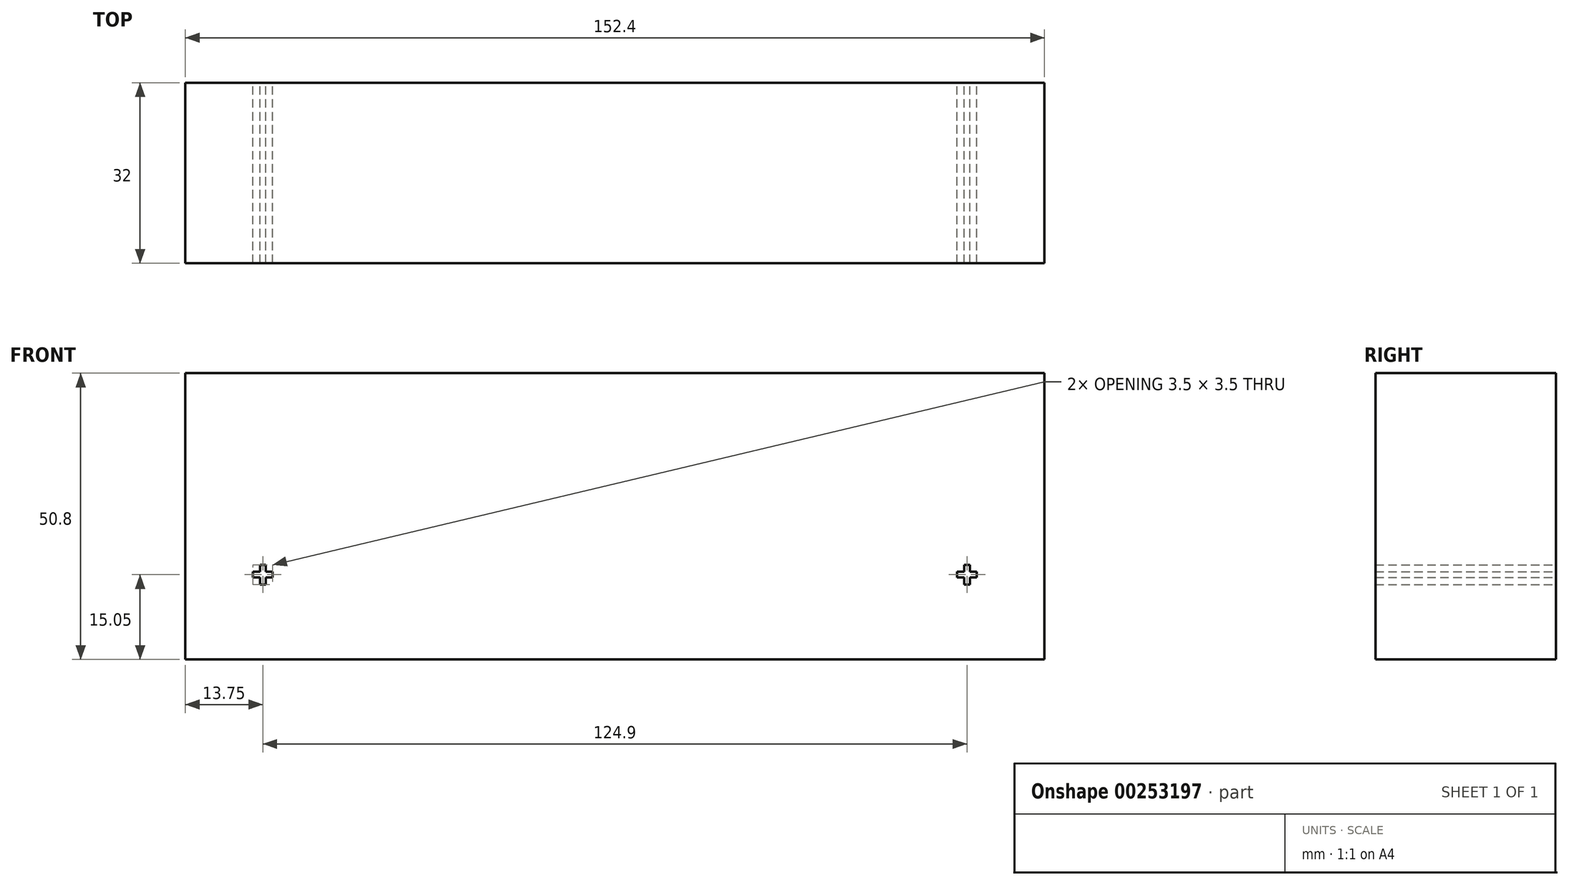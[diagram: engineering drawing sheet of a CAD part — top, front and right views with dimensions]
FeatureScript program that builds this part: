
annotation { "Feature Type Name" : "Feature", "Feature Type Description" : "" }
export const myFeature = defineFeature(function(context is Context, id is Id, definition is map)
    precondition{}
    {
        {
            var Q0;
            Q0=qCreatedBy(makeId("Front.planeOp"),FACE);
            var sketch = newSketch(context, id + "F0", { "sketchPlane" : qUnion([Q0])});
            skLineSegment(sketch, "E0.bottom", {"start": v(76.2, 25.4) * mm, "end": v(-76.2, 25.4) * mm});
            skLineSegment(sketch, "E0.top", {"start": v(76.2, -25.4) * mm, "end": v(-76.2, -25.4) * mm});
            skLineSegment(sketch, "E0.left", {"start": v(76.2, 25.4) * mm, "end": v(76.2, -25.4) * mm});
            skLineSegment(sketch, "E0.right", {"start": v(-76.2, 25.4) * mm, "end": v(-76.2, -25.4) * mm});
            skPoint(sketch, "E0.middle", {"position": v(0, 0) * mm});
            skLineSegment(sketch, "E1.0", {"start": v(61.95, -9.85) * mm, "end": v(61.95, -8.6) * mm});
            skLineSegment(sketch, "E1.1", {"start": v(61.95, -8.6) * mm, "end": v(62.95, -8.6) * mm});
            skLineSegment(sketch, "E1.2", {"start": v(62.95, -8.6) * mm, "end": v(62.95, -9.85) * mm});
            skLineSegment(sketch, "E1.3", {"start": v(62.95, -9.85) * mm, "end": v(64.2, -9.85) * mm});
            skLineSegment(sketch, "E1.4", {"start": v(64.2, -9.85) * mm, "end": v(64.2, -10.85) * mm});
            skLineSegment(sketch, "E1.5", {"start": v(64.2, -10.85) * mm, "end": v(62.95, -10.85) * mm});
            skLineSegment(sketch, "E1.6", {"start": v(62.95, -10.85) * mm, "end": v(62.95, -12.1) * mm});
            skLineSegment(sketch, "E1.7", {"start": v(62.95, -12.1) * mm, "end": v(61.95, -12.1) * mm});
            skLineSegment(sketch, "E1.8", {"start": v(61.95, -12.1) * mm, "end": v(61.95, -10.85) * mm});
            skLineSegment(sketch, "E1.9", {"start": v(61.95, -10.85) * mm, "end": v(60.7, -10.85) * mm});
            skLineSegment(sketch, "E1.10", {"start": v(60.7, -10.85) * mm, "end": v(60.7, -9.85) * mm});
            skLineSegment(sketch, "E1.11", {"start": v(60.7, -9.85) * mm, "end": v(61.95, -9.85) * mm});
            skLineSegment(sketch, "E2", {"start": v(0, 25.4) * mm, "end": v(0, 0) * mm, "construction": true});
            skLineSegment(sketch, "E3.MirrorCS", {"start": v(-62.95, -8.6) * mm, "end": v(-62.95, -9.85) * mm});
            skLineSegment(sketch, "E4.MirrorCS", {"start": v(-61.95, -8.6) * mm, "end": v(-62.95, -8.6) * mm});
            skLineSegment(sketch, "E5.MirrorCS", {"start": v(-61.95, -9.85) * mm, "end": v(-61.95, -8.6) * mm});
            skLineSegment(sketch, "E6.MirrorCS", {"start": v(-60.7, -9.85) * mm, "end": v(-61.95, -9.85) * mm});
            skLineSegment(sketch, "E7.MirrorCS", {"start": v(-61.95, -10.85) * mm, "end": v(-60.7, -10.85) * mm});
            skLineSegment(sketch, "E8.MirrorCS", {"start": v(-61.95, -12.1) * mm, "end": v(-61.95, -10.85) * mm});
            skLineSegment(sketch, "E9.MirrorCS", {"start": v(-60.7, -10.85) * mm, "end": v(-60.7, -9.85) * mm});
            skLineSegment(sketch, "E10.MirrorCS", {"start": v(-62.95, -12.1) * mm, "end": v(-61.95, -12.1) * mm});
            skLineSegment(sketch, "E11.MirrorCS", {"start": v(-62.95, -10.85) * mm, "end": v(-62.95, -12.1) * mm});
            skLineSegment(sketch, "E12.MirrorCS", {"start": v(-64.2, -10.85) * mm, "end": v(-62.95, -10.85) * mm});
            skLineSegment(sketch, "E13.MirrorCS", {"start": v(-64.2, -9.85) * mm, "end": v(-64.2, -10.85) * mm});
            skLineSegment(sketch, "E14.MirrorCS", {"start": v(-62.95, -9.85) * mm, "end": v(-64.2, -9.85) * mm});
            skSolve(sketch);
        }
        {
            var Q0;
            Q0 = qSketchRegion(id + "F0", true);
            extrude(context, id + "F1", {"entities" : qUnion([Q0]), "depth" : 32 * mm});
        }
    });
